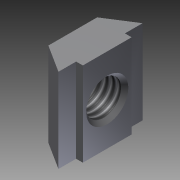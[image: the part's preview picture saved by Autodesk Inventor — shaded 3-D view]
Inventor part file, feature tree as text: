
AUTODESK INVENTOR PART (.ipt)
format: ipt  version: 2013 (Build 170138000, 138)  size: 113,152 bytes
history: native  units: mm
features: other x21, sketch x2, extrude x1, revolve x1, thread x1
ambient origin geometry x8: Origin, YZ Plane, XZ Plane, XY Plane, X Axis, Y Axis, Z Axis, Center Point
bodies: Solid1 (feature_tree)
feature tree (26):
  extrude  "Extrusion1"  TaperAngle=360.0deg  [1 undecoded]
  revolve  "Revolution1"  [1 undecoded]
  thread  "Thread1"  [1 undecoded]
  other  "nut_XY"
  other  "nut_YZ"
  other  "nut_ZX"
  other  "nut_X"
  other  "nut_Y"
  other  "nut_Z"
  other  "nut_Center"
  other  "to_bolt_XY"
  other  "to_bolt_YZ"
  other  "to_bolt_ZX"
  other  "to_bolt_X"
  other  "to_bolt_Y"
  other  "to_bolt_Z"
  other  "to_bolt_Center"
  other  "to_frames_XY"
  other  "to_frames_YZ"
  other  "to_frames_ZX"
  other  "to_frames_X"
  other  "to_frames_Y"
  other  "to_frames_Z"
  other  "to_frames_Center"
  sketch  "Sketch_4"  dims[d0=10.0mm d1=0.0mm d2=360.0deg]
  sketch  "Sketch_5"  dims[d3=3.234mm d4=0.0mm]
note: 3 required parameter values undecoded (feature->parameter linkage not recoverable at this tier; creation-order binding heuristic only, values carry confidence <= 0.55)
